# Revit family: Haworth_Planes_HeightAdjustBench_SingleSided
name_source: partatom
category: Furniture Systems
revit_build: Autodesk Revit 2018 (Build: 20170223_1515(x64)
units: mm (PartAtom-declared; Revit-internal decimal feet)

## family parameters
Always vertical = Yes
Cut with Voids When Loaded = No
OmniClass Number = 23.40.70.14.64.21
OmniClass Title = Systems Furniture
Part Type = Normal
Room Calculation Point = No
Round Connector Dimension = Use Diameter
Shared = No
Work Plane-Based = No

## types (4) — shared parameters
Actual Height = 31"
Assembly Code = E2020200
Base Tube Finish = Haworth _ Paint _ Black
Box Body Finish = Haworth _ Paint _ Black
Crank Offset = 14 1/8"
Custom Size = No
Edgeband = Yes
Gap Depth = 3 11/16"
Height = 31"
J-Rail Height = 22 5/8"
Knife Edge = No
Leg Height = 29 13/16"
Leg Offset = 10"
Lever Depth = 12"
Manufacturer = Haworth
Max. Depth = 30"
Max. Height = 46"
Max. Overall Depth = 33 3/8"
Max. Width = 70"
Min. Depth = 23"
Min. Height = 27"
Min. Overall Depth = 30 7/16"
Min. Width = 46"
Min/Max Width = 46-70 in. @ 6 in. increment
Model = TARA
Revision Number = 2
Size = Verify Final Dim. w/ Haworth
Standard Overall Depth = 30 7/16, 33 3/8 in.
Standard Worksurface Depth = 23, 24, 29, 30 in.
Table Thickness = 1 3/16"
Trim Finish = Haworth _ Paint _ Metallic Champagne
URL = www.haworth.com
URL - Product = https://www.haworth.com
Warranty = https://www.haworth.com

## per-type parameters (varying)
| type | Actual Depth | Actual Overall Depth | Actual Width | Depth | Depth 23 | Depth 29 | Description | Electric Adjustment | Hand Crank | J-Rail Width | Leg Side Offset | Width |
| 70w 30d - Electric Adjustment | 30" | 33 11/16" | 70" | 30" | No | Yes | Haworth - Planes HAT Bench - Single-Sided - 70w 30d - Electric Adjustment | Yes | No | 57 5/8" | 28 13/16" | 70" |
| 70w 30d - Crank Adjustment | 30" | 33 11/16" | 70" | 30" | No | Yes | Haworth - Planes HAT Bench - Single-Sided - 70w 30d - Crank Adjustment | No | Yes | 57 5/8" | 28 13/16" | 70" |
| 46w 23d - Crank Adjustment | 23" | 26 11/16" | 46" | 23" | Yes | No | Haworth - Planes HAT Bench - Single-Sided - 46w 23d - Crank Adjustment | No | Yes | 33 5/8" | 16 13/16" | 46" |
| 58w 24d - Electric Adjustment | 24" | 27 11/16" | 58" | 24" | Yes | No | Haworth - Planes HAT Bench - Single-Sided - 58w 24d - Electric Adjustment | Yes | No | 45 5/8" | 22 13/16" | 58" |

## geometry (parser evidence)
native form markers: Extrusion x1, Sweep x12
no freeform markers — native parametric forms only
